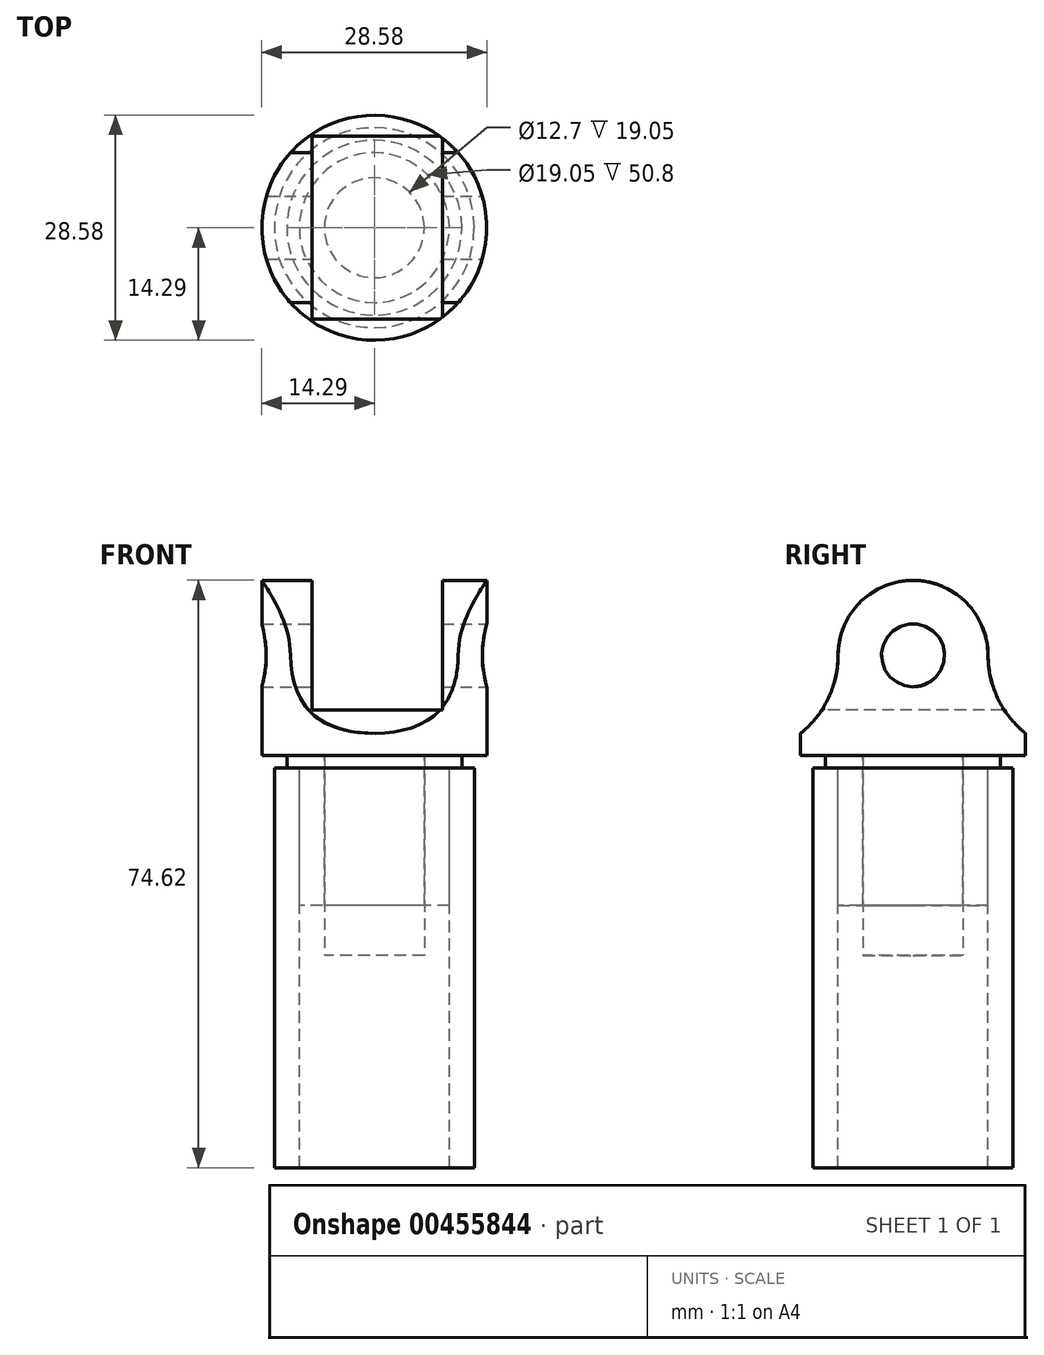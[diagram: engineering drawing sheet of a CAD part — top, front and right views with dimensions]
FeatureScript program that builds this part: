
annotation { "Feature Type Name" : "Feature", "Feature Type Description" : "" }
export const myFeature = defineFeature(function(context is Context, id is Id, definition is map)
    precondition{}
    {
        {
            var Q0;
            Q0=qCreatedBy(makeId("Top.planeOp"),FACE);
            var sketch = newSketch(context, id + "F0", { "sketchPlane" : qUnion([Q0])});
            skCircle(sketch, "E0", {"center": v(0, 0) * mm, "radius": 6.35 * mm});
            skSolve(sketch);
        }
        {
            var Q0;
            Q0=makeQuery(id+"F0.imprint","IMPRINT",FACE,{"disambiguationData":[TD([[makeQuery(id+"F0.imprint","IMPRINT",EDGE,{"derivedFrom":sQuery(id+"F0.wireOp",EDGE,"E0")}),1.0]])]});
            extrude(context, id + "F1", {"entities" : qUnion([Q0]), "depth" : 25.4 * mm});
        }
        {
            var Q0;
            Q0=makeQuery(id+"F1.opExtrude","CAP_FACE",FACE,{"disambiguationData":[OSD([sQuery(id+"F0.wireOp",EDGE,"E0")])],"isStart":false});
            var sketch = newSketch(context, id + "F2", { "sketchPlane" : qUnion([Q0])});
            skCircle(sketch, "E1", {"center": v(0, 0) * mm, "radius": 11.11 * mm});
            skCircle(sketch, "E2", {"center": v(0, 0) * mm, "radius": 9.52 * mm});
            skCircle(sketch, "E3", {"center": v(0, 0) * mm, "radius": 6.35 * mm});
            skSolve(sketch);
        }
        {
            var Q0;
            Q0=makeQuery(id+"F2.imprint","IMPRINT",FACE,{"disambiguationData":[TD([[makeQuery(id+"F2.imprint","IMPRINT",EDGE,{"derivedFrom":sQuery(id+"F2.wireOp",EDGE,"E2")}),1.0]])]});
            extrude(context, id + "F3", {"entities" : qUnion([Q0]), "oppositeDirection" : true, "depth" : 19.05 * mm});
        }
        {
            var Q0;
            Q0=makeQuery(id+"F2.imprint","IMPRINT",FACE,{"disambiguationData":[TD([[makeQuery(id+"F2.imprint","IMPRINT",EDGE,{"derivedFrom":sQuery(id+"F2.wireOp",EDGE,"E1")}),1.0]])]});
            extrude(context, id + "F4", {"entities" : qUnion([Q0]), "operationType" : NewBodyOperationType.ADD, "oppositeDirection" : true, "depth" : 1.59 * mm});
        }
        {
            var Q0;
            Q0=makeQuery(id+"F4.opExtrude","CAP_FACE",FACE,{"disambiguationData":[OSD([sQuery(id+"F2.wireOp",EDGE,"E1"),sQuery(id+"F2.wireOp",EDGE,"E2")])],"isStart":false});
            var sketch = newSketch(context, id + "F5", { "sketchPlane" : qUnion([Q0])});
            skCircle(sketch, "E4", {"center": v(0, 0) * mm, "radius": 12.7 * mm});
            skCircle(sketch, "E5", {"center": v(0, 0) * mm, "radius": 9.53 * mm});
            skSolve(sketch);
        }
        {
            var Q0;
            Q0 = qSketchRegion(id + "F5", true);
            extrude(context, id + "F6", {"entities" : qUnion([Q0]), "depth" : 50.8 * mm});
        }
        {
            var Q0;
            Q0=makeQuery(id+"F2.imprint","IMPRINT",FACE,{"disambiguationData":[TD([[makeQuery(id+"F2.imprint","IMPRINT",EDGE,{"derivedFrom":sQuery(id+"F2.wireOp",EDGE,"E3")}),1.0]])]});
            var sketch = newSketch(context, id + "F7", { "sketchPlane" : qUnion([Q0])});
            skCircle(sketch, "E6", {"center": v(0, 0) * mm, "radius": 14.29 * mm});
            skSolve(sketch);
        }
        {
            var Q0;
            Q0 = qSketchRegion(id + "F7", true);
            extrude(context, id + "F8", {"entities" : qUnion([Q0]), "depth" : 25.4 * mm});
        }
        {
            var Q0;
            Q0=qCreatedBy(makeId("Right.planeOp"),FACE);
            var sketch = newSketch(context, id + "F9", { "sketchPlane" : qUnion([Q0])});
            skCircle(sketch, "E7", {"center": v(0, 38.1) * mm, "radius": 4 * mm});
            skArc(sketch, "E8", {"start": v(9.53, 38.1) * mm, "mid": v(0, 47.62) * mm, "end": v(-9.53, 38.1) * mm});
            skArc(sketch, "E9", {"start": v(9.53, 38.1) * mm, "mid": v(22.23, 25.4) * mm, "end": v(34.93, 38.1) * mm});
            skArc(sketch, "E10", {"start": v(-34.93, 38.1) * mm, "mid": v(-22.23, 25.4) * mm, "end": v(-9.53, 38.1) * mm});
            skLineSegment(sketch, "E11", {"start": v(44.06, 38.1) * mm, "end": v(-50.21, 38.1) * mm, "construction": true});
            skLineSegment(sketch, "E12", {"start": v(34.93, 38.1) * mm, "end": v(34.93, 62.9) * mm});
            skLineSegment(sketch, "E13", {"start": v(34.93, 62.9) * mm, "end": v(-34.93, 62.9) * mm});
            skLineSegment(sketch, "E14", {"start": v(-34.93, 62.9) * mm, "end": v(-34.93, 38.1) * mm});
            skSolve(sketch);
        }
        {
            var Q0;
            Q0 = qSketchRegion(id + "F9", true);
            extrude(context, id + "F10", {"entities" : qUnion([Q0]), "operationType" : NewBodyOperationType.REMOVE, "oppositeDirection" : true, "depth" : 25.4 * mm, "hasSecondDirection" : true, "secondDirectionOppositeDirection" : false, "secondDirectionDepth" : 25.4 * mm});
        }
        {
            var Q0;
            Q0=qCreatedBy(makeId("Front.planeOp"),FACE);
            var sketch = newSketch(context, id + "F11", { "sketchPlane" : qUnion([Q0])});
            skLineSegment(sketch, "E15.bottom", {"start": v(-7.87, 52.54) * mm, "end": v(8.64, 52.54) * mm});
            skLineSegment(sketch, "E15.top", {"start": v(-7.87, 31.13) * mm, "end": v(8.64, 31.13) * mm});
            skLineSegment(sketch, "E15.left", {"start": v(-7.87, 52.54) * mm, "end": v(-7.87, 31.13) * mm});
            skLineSegment(sketch, "E15.right", {"start": v(8.64, 52.54) * mm, "end": v(8.64, 31.13) * mm});
            skSolve(sketch);
        }
        {
            var Q0;
            Q0 = qSketchRegion(id + "F11", true);
            extrude(context, id + "F12", {"entities" : qUnion([Q0]), "operationType" : NewBodyOperationType.REMOVE, "oppositeDirection" : true, "depth" : 25.4 * mm, "hasSecondDirection" : true, "secondDirectionOppositeDirection" : false, "secondDirectionDepth" : 25.4 * mm});
        }
    });
